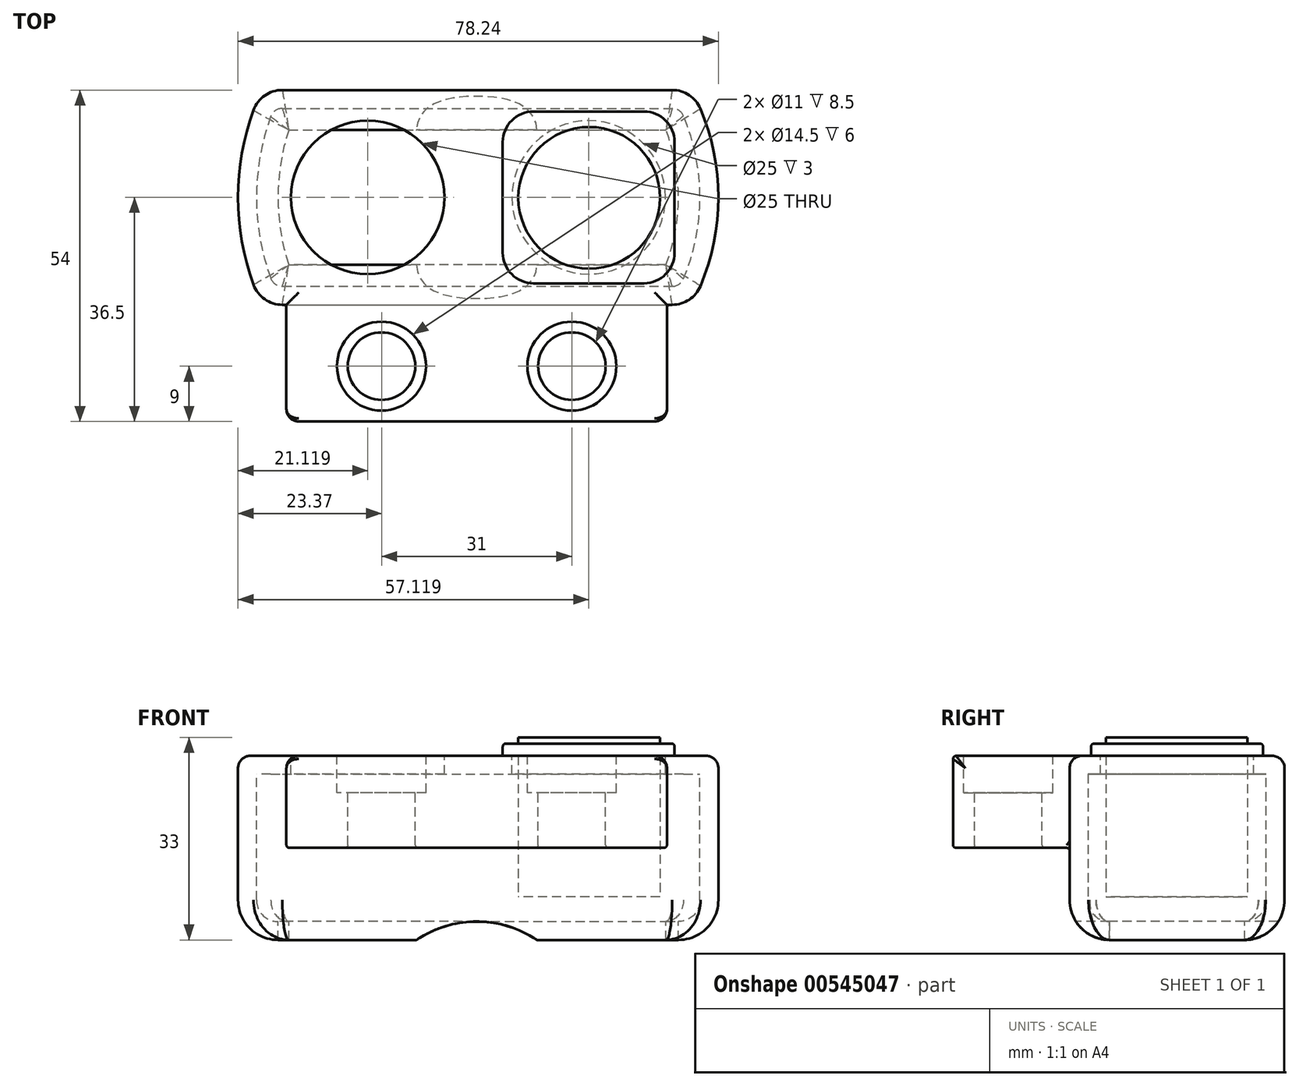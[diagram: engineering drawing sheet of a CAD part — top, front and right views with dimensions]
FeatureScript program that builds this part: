
annotation { "Feature Type Name" : "Feature", "Feature Type Description" : "" }
export const myFeature = defineFeature(function(context is Context, id is Id, definition is map)
    precondition{}
    {
        {
            var Q0;
            Q0=qCreatedBy(makeId("Front.planeOp"),FACE);
            var sketch = newSketch(context, id + "F0", { "sketchPlane" : qUnion([Q0])});
            skLineSegment(sketch, "E0.bottom", {"start": v(0, 0) * mm, "end": v(70, 0) * mm});
            skLineSegment(sketch, "E0.top", {"start": v(0, -30) * mm, "end": v(70, -30) * mm});
            skLineSegment(sketch, "E0.left", {"start": v(0, 0) * mm, "end": v(0, -30) * mm});
            skLineSegment(sketch, "E0.right", {"start": v(70, 0) * mm, "end": v(70, -30) * mm});
            skSolve(sketch);
        }
        {
            var Q0;
            Q0=qSketchRegion(id+"F0",true);
            extrude(context, id + "F1", {"entities" : qUnion([Q0]), "depth" : 20 * mm, "offsetDistance" : 25 * mm, "hasSecondDirection" : true, "secondDirectionOppositeDirection" : true, "secondDirectionDepth" : 15 * mm});
        }
        {
            var Q0;
            Q0=makeQuery(id+"F1.opExtrude","SWEPT_FACE",FACE,{"disambiguationData":[OSD([sQuery(id+"F0.wireOp",EDGE,"E0.bottom")])]});
            var sketch = newSketch(context, id + "F2", { "sketchPlane" : qUnion([Q0])});
            skArc(sketch, "E1", {"start": v(0, 15) * mm, "mid": v(-3.87, -2.5) * mm, "end": v(0, -20) * mm});
            skLineSegment(sketch, "E2", {"start": v(0, 15) * mm, "end": v(0, -20) * mm});
            skLineSegment(sketch, "E3", {"start": v(70, 15) * mm, "end": v(70, -20) * mm});
            skArc(sketch, "E4.trimOffspring", {"start": v(70, -20) * mm, "mid": v(74.37, -2.5) * mm, "end": v(70, 15) * mm});
            skSolve(sketch);
        }
        {
            var Q0;
            Q0=qSketchRegion(id+"F2",true);
            extrude(context, id + "F3", {"entities" : qUnion([Q0]), "operationType" : NewBodyOperationType.ADD, "oppositeDirection" : true, "depth" : 30 * mm, "offsetDistance" : 25 * mm});
        }
        {
            var Q0;
            Q0=makeQuery(id+"FqyKaclqLz1FDZU_1.boolean.opBoolean","MERGE",FACE,{"derivedFrom":[makeQuery(id+"F1.opExtrude","SWEPT_FACE",FACE,{"disambiguationData":[OSD([sQuery(id+"F0.wireOp",EDGE,"E0.top")])]}),makeQuery(id+"FqyKaclqLz1FDZU_1.opExtrude","CAP_FACE",FACE,{"disambiguationData":[OSD([sQuery(id+"FIyjTsEw3E9njMs_1.wireOp",EDGE,"glMM5qbk-qYOk-jkf3-kfGg-ePqJmBg5fgPB"),sQuery(id+"FIyjTsEw3E9njMs_1.wireOp",EDGE,"cEUHAI24-cV1s-2wJQ-DF9F-RTduI9zPpPZA")])],"isStart":false}),makeQuery(id+"FqyKaclqLz1FDZU_1.opExtrude","CAP_FACE",FACE,{"disambiguationData":[OSD([sQuery(id+"FIyjTsEw3E9njMs_1.wireOp",EDGE,"fG08fdOo-hFZ7-qGUP-nEzv-jywKs9Jv7XxH"),sQuery(id+"FIyjTsEw3E9njMs_1.wireOp",EDGE,"jPeKVb5Y-i3kR-RX1O-jRN1-yy8WQ1SG1LOX")])],"isStart":false})]});
            fillet(context, id + "F4", {"entities" : qUnion([Q0]), "radius" : 6.5 * mm, "tangentPropagation" : true, "allowEdgeOverflow" : false});
        }
        {
            var Q0;
            Q0=makeQuery(id+"FqyKaclqLz1FDZU_1.boolean.opBoolean","MERGE",FACE,{"derivedFrom":[makeQuery(id+"F1.opExtrude","SWEPT_FACE",FACE,{"disambiguationData":[OSD([sQuery(id+"F0.wireOp",EDGE,"E0.top")])]}),makeQuery(id+"FqyKaclqLz1FDZU_1.opExtrude","CAP_FACE",FACE,{"disambiguationData":[OSD([sQuery(id+"FIyjTsEw3E9njMs_1.wireOp",EDGE,"glMM5qbk-qYOk-jkf3-kfGg-ePqJmBg5fgPB"),sQuery(id+"FIyjTsEw3E9njMs_1.wireOp",EDGE,"cEUHAI24-cV1s-2wJQ-DF9F-RTduI9zPpPZA")])],"isStart":false}),makeQuery(id+"FqyKaclqLz1FDZU_1.opExtrude","CAP_FACE",FACE,{"disambiguationData":[OSD([sQuery(id+"FIyjTsEw3E9njMs_1.wireOp",EDGE,"fG08fdOo-hFZ7-qGUP-nEzv-jywKs9Jv7XxH"),sQuery(id+"FIyjTsEw3E9njMs_1.wireOp",EDGE,"jPeKVb5Y-i3kR-RX1O-jRN1-yy8WQ1SG1LOX")])],"isStart":false})]});
            shell(context, id + "F5", {"entities" : qUnion([Q0]), "thickness" : 3 * mm});
        }
        {
            var Q0;
            Q0=makeQuery(id+"F1.opExtrude","CAP_FACE",FACE,{"disambiguationData":[OSD([sQuery(id+"F0.wireOp",EDGE,"E0.bottom"),sQuery(id+"F0.wireOp",EDGE,"E0.top"),sQuery(id+"F0.wireOp",EDGE,"E0.left"),sQuery(id+"F0.wireOp",EDGE,"E0.right")])],"isStart":false});
            var sketch = newSketch(context, id + "F6", { "sketchPlane" : qUnion([Q0])});
            skLineSegment(sketch, "E5.bottom", {"start": v(4, 0) * mm, "end": v(66, 0) * mm});
            skLineSegment(sketch, "E5.top", {"start": v(4, -15) * mm, "end": v(66, -15) * mm});
            skLineSegment(sketch, "E5.left", {"start": v(4, 0) * mm, "end": v(4, -15) * mm});
            skLineSegment(sketch, "E5.right", {"start": v(66, 0) * mm, "end": v(66, -15) * mm});
            skSolve(sketch);
        }
        {
            var Q0;
            Q0=makeQuery(id+"F6.imprint","IMPRINT",FACE,{"disambiguationData":[TD([[makeQuery(id+"F6.imprint","IMPRINT",EDGE,{"derivedFrom":sQuery(id+"F6.wireOp",EDGE,"E5.bottom")}),-1.0]])]});
            extrude(context, id + "F7", {"entities" : qUnion([Q0]), "operationType" : NewBodyOperationType.ADD, "depth" : 19 * mm, "offsetDistance" : 25 * mm});
        }
        {
            var Q0;
            {var subQ0=sQuery(id+"FIyjTsEw3E9njMs_1.wireOp",EDGE,"jPeKVb5Y-i3kR-RX1O-jRN1-yy8WQ1SG1LOX");var subQ1=sQuery(id+"FIyjTsEw3E9njMs_1.wireOp",EDGE,"fG08fdOo-hFZ7-qGUP-nEzv-jywKs9Jv7XxH");var subQ2=sQuery(id+"F0.wireOp",EDGE,"E0.bottom");Q0=makeQuery(id+"FqyKaclqLz1FDZU_1.boolean.opBoolean","MERGE",EDGE,{"derivedFrom":[makeQuery(id+"F1.opExtrude","CAP_EDGE",EDGE,{"disambiguationData":[OSD([sQuery(id+"F0.wireOp",EDGE,"E0.right")])],"isStart":false}),makeQuery(id+"FqyKaclqLz1FDZU_1.opExtrude","SWEPT_EDGE",EDGE,{"disambiguationData":[OSD([subQ2,subQ1,subQ0]),TDD([makeQuery(id+"FIyjTsEw3E9njMs_1.imprint","INTERSECT",VERTEX,{"derivedFrom":[makeQuery(id+"F2.imprint","IMPRINT",EDGE,{"derivedFrom":makeQuery(id+"F1.opExtrude","CAP_EDGE",EDGE,{"disambiguationData":[OSD([subQ2])],"isStart":false})}),subQ1,subQ0]})])]})]});}
            var Q1;
            {var subQ0=sQuery(id+"FIyjTsEw3E9njMs_1.wireOp",EDGE,"cEUHAI24-cV1s-2wJQ-DF9F-RTduI9zPpPZA");var subQ1=sQuery(id+"FIyjTsEw3E9njMs_1.wireOp",EDGE,"glMM5qbk-qYOk-jkf3-kfGg-ePqJmBg5fgPB");var subQ2=sQuery(id+"F0.wireOp",EDGE,"E0.bottom");Q1=makeQuery(id+"FqyKaclqLz1FDZU_1.boolean.opBoolean","MERGE",EDGE,{"derivedFrom":[makeQuery(id+"F1.opExtrude","CAP_EDGE",EDGE,{"disambiguationData":[OSD([sQuery(id+"F0.wireOp",EDGE,"E0.left")])],"isStart":false}),makeQuery(id+"FqyKaclqLz1FDZU_1.opExtrude","SWEPT_EDGE",EDGE,{"disambiguationData":[OSD([subQ2,subQ1,subQ0]),TDD([makeQuery(id+"FIyjTsEw3E9njMs_1.imprint","INTERSECT",VERTEX,{"derivedFrom":[makeQuery(id+"F2.imprint","IMPRINT",EDGE,{"derivedFrom":makeQuery(id+"F1.opExtrude","CAP_EDGE",EDGE,{"disambiguationData":[OSD([subQ2])],"isStart":false})}),subQ1,subQ0]})])]})]});}
            var Q2;
            {var subQ0=sQuery(id+"FIyjTsEw3E9njMs_1.wireOp",EDGE,"jPeKVb5Y-i3kR-RX1O-jRN1-yy8WQ1SG1LOX");var subQ1=sQuery(id+"FIyjTsEw3E9njMs_1.wireOp",EDGE,"fG08fdOo-hFZ7-qGUP-nEzv-jywKs9Jv7XxH");var subQ2=sQuery(id+"F0.wireOp",EDGE,"E0.bottom");Q2=makeQuery(id+"FqyKaclqLz1FDZU_1.boolean.opBoolean","MERGE",EDGE,{"derivedFrom":[makeQuery(id+"F1.opExtrude","CAP_EDGE",EDGE,{"disambiguationData":[OSD([sQuery(id+"F0.wireOp",EDGE,"E0.right")])],"isStart":true}),makeQuery(id+"FqyKaclqLz1FDZU_1.opExtrude","SWEPT_EDGE",EDGE,{"disambiguationData":[OSD([subQ2,subQ1,subQ0]),TDD([makeQuery(id+"FIyjTsEw3E9njMs_1.imprint","INTERSECT",VERTEX,{"derivedFrom":[makeQuery(id+"F2.imprint","IMPRINT",EDGE,{"derivedFrom":makeQuery(id+"F1.opExtrude","CAP_EDGE",EDGE,{"disambiguationData":[OSD([subQ2])],"isStart":true})}),subQ1,subQ0]})])]})]});}
            var Q3;
            {var subQ0=sQuery(id+"FIyjTsEw3E9njMs_1.wireOp",EDGE,"cEUHAI24-cV1s-2wJQ-DF9F-RTduI9zPpPZA");var subQ1=sQuery(id+"FIyjTsEw3E9njMs_1.wireOp",EDGE,"glMM5qbk-qYOk-jkf3-kfGg-ePqJmBg5fgPB");var subQ2=sQuery(id+"F0.wireOp",EDGE,"E0.bottom");Q3=makeQuery(id+"FqyKaclqLz1FDZU_1.boolean.opBoolean","MERGE",EDGE,{"derivedFrom":[makeQuery(id+"F1.opExtrude","CAP_EDGE",EDGE,{"disambiguationData":[OSD([sQuery(id+"F0.wireOp",EDGE,"E0.left")])],"isStart":true}),makeQuery(id+"FqyKaclqLz1FDZU_1.opExtrude","SWEPT_EDGE",EDGE,{"disambiguationData":[OSD([subQ2,subQ1,subQ0]),TDD([makeQuery(id+"FIyjTsEw3E9njMs_1.imprint","INTERSECT",VERTEX,{"derivedFrom":[makeQuery(id+"F2.imprint","IMPRINT",EDGE,{"derivedFrom":makeQuery(id+"F1.opExtrude","CAP_EDGE",EDGE,{"disambiguationData":[OSD([subQ2])],"isStart":true})}),subQ1,subQ0]})])]})]});}
            fillet(context, id + "F8", {"entities" : qUnion([Q0, Q1, Q2, Q3]), "radius" : 5 * mm, "tangentPropagation" : true, "allowEdgeOverflow" : false});
        }
        {
            var Q0;
            Q0=makeQuery(id+"FUNl6TjWTGiayeX_1.boolean.opBoolean","MERGE",FACE,{"derivedFrom":[makeQuery(id+"FqyKaclqLz1FDZU_1.boolean.opBoolean","MERGE",FACE,{"derivedFrom":[makeQuery(id+"F1.opExtrude","SWEPT_FACE",FACE,{"disambiguationData":[OSD([sQuery(id+"F0.wireOp",EDGE,"E0.bottom")])]}),makeQuery(id+"FqyKaclqLz1FDZU_1.opExtrude","CAP_FACE",FACE,{"disambiguationData":[OSD([sQuery(id+"FIyjTsEw3E9njMs_1.wireOp",EDGE,"glMM5qbk-qYOk-jkf3-kfGg-ePqJmBg5fgPB"),sQuery(id+"FIyjTsEw3E9njMs_1.wireOp",EDGE,"cEUHAI24-cV1s-2wJQ-DF9F-RTduI9zPpPZA")])],"isStart":true}),makeQuery(id+"FqyKaclqLz1FDZU_1.opExtrude","CAP_FACE",FACE,{"disambiguationData":[OSD([sQuery(id+"FIyjTsEw3E9njMs_1.wireOp",EDGE,"fG08fdOo-hFZ7-qGUP-nEzv-jywKs9Jv7XxH"),sQuery(id+"FIyjTsEw3E9njMs_1.wireOp",EDGE,"jPeKVb5Y-i3kR-RX1O-jRN1-yy8WQ1SG1LOX")])],"isStart":true})]}),makeQuery(id+"FUNl6TjWTGiayeX_1.opExtrude","SWEPT_FACE",FACE,{"disambiguationData":[OSD([sQuery(id+"Fp4lW6qHkl5UULX_1.wireOp",EDGE,"Grlhg8hl-7fqz-5gtc-eQS2-KlK7X2J6LcNq.bottom")])]})]});
            var sketch = newSketch(context, id + "F9", { "sketchPlane" : qUnion([Q0])});
            skPoint(sketch, "E6", {"position": v(19.5, -30) * mm});
            skPoint(sketch, "E7", {"position": v(50.5, -30) * mm});
            skLineSegment(sketch, "E8", {"start": v(66, -30) * mm, "end": v(50.5, -30) * mm});
            skLineSegment(sketch, "E9.trimOffspring", {"start": v(19.5, -30) * mm, "end": v(4, -30) * mm});
            skSolve(sketch);
        }
        {
            var Q0;
            Q0=sQuery(id+"F9.wireOp",VERTEX,"E6");
            var Q1;
            Q1=sQuery(id+"F9.wireOp",VERTEX,"E7");
            var Q2;
            Q2=makeQuery(id+"F1.opExtrude","SWEPT_BODY",BODY,{"disambiguationData":[OSD([sQuery(id+"F0.wireOp",EDGE,"E0.bottom"),sQuery(id+"F0.wireOp",EDGE,"E0.top"),sQuery(id+"F0.wireOp",EDGE,"E0.left"),sQuery(id+"F0.wireOp",EDGE,"E0.right")])]});
            hole(context, id + "F10", {"style" : HoleStyle.C_BORE, "endStyle" : HoleEndStyle.THROUGH, "holeDiameter" : 11 * mm, "cBoreDiameter" : 14.5 * mm, "cBoreDepth" : 6 * mm, "isTappedThrough" : true, "tappedDepth" : 12 * mm, "tapClearance" : 3, "startFromSketch" : true, "locations" : qUnion([Q0, Q1]), "scope" : qUnion([Q2])});
        }
        {
            var Q0;
            {var subQ0=sQuery(id+"F0.wireOp",EDGE,"E0.bottom");Q0=makeQuery(id+"F2.imprint","IMPRINT",FACE,{"disambiguationData":[TD([[makeQuery(id+"F2.imprint","IMPRINT",EDGE,{"derivedFrom":makeQuery(id+"F1.opExtrude","CAP_EDGE",EDGE,{"disambiguationData":[OSD([subQ0])],"isStart":true})}),-1.0]])]});}
            var sketch = newSketch(context, id + "F11", { "sketchPlane" : qUnion([Q0])});
            skLineSegment(sketch, "E10", {"start": v(-3.87, -2.5) * mm, "end": v(17.25, -2.5) * mm});
            skPoint(sketch, "E11", {"position": v(17.25, -2.5) * mm});
            skPoint(sketch, "E12", {"position": v(53.25, -2.5) * mm});
            skLineSegment(sketch, "E13.trimOffspring", {"start": v(53.25, -2.5) * mm, "end": v(74.37, -2.5) * mm});
            skSolve(sketch);
        }
        {
            var Q0;
            Q0=sQuery(id+"F11.wireOp",VERTEX,"E11");
            var Q1;
            Q1=sQuery(id+"F11.wireOp",VERTEX,"E12");
            var Q2;
            Q2=makeQuery(id+"F1.opExtrude","SWEPT_BODY",BODY,{"disambiguationData":[OSD([sQuery(id+"F0.wireOp",EDGE,"E0.bottom"),sQuery(id+"F0.wireOp",EDGE,"E0.top"),sQuery(id+"F0.wireOp",EDGE,"E0.left"),sQuery(id+"F0.wireOp",EDGE,"E0.right")])]});
            hole(context, id + "F12", {"style" : HoleStyle.SIMPLE, "endStyle" : HoleEndStyle.BLIND, "holeDiameter" : 25 * mm, "holeDepth" : 10 * mm, "isTappedThrough" : true, "tappedDepth" : 12 * mm, "tapClearance" : 3, "startFromSketch" : true, "locations" : qUnion([Q0, Q1]), "scope" : qUnion([Q2])});
        }
        {
            var Q0;
            Q0=makeQuery(id+"F1.opExtrude","CAP_FACE",FACE,{"disambiguationData":[OSD([sQuery(id+"F0.wireOp",EDGE,"E0.bottom"),sQuery(id+"F0.wireOp",EDGE,"E0.top"),sQuery(id+"F0.wireOp",EDGE,"E0.left"),sQuery(id+"F0.wireOp",EDGE,"E0.right")])],"isStart":false});
            var sketch = newSketch(context, id + "F13", { "sketchPlane" : qUnion([Q0])});
            skPoint(sketch, "E14", {"position": v(35, -44.5) * mm});
            skLineSegment(sketch, "E15", {"start": v(35, 0) * mm, "end": v(35, -44.5) * mm});
            skSolve(sketch);
        }
        {
            var Q0;
            Q0=sQuery(id+"F13.wireOp",VERTEX,"E14");
            var Q1;
            Q1=makeQuery(id+"F1.opExtrude","SWEPT_BODY",BODY,{"disambiguationData":[OSD([sQuery(id+"F0.wireOp",EDGE,"E0.bottom"),sQuery(id+"F0.wireOp",EDGE,"E0.top"),sQuery(id+"F0.wireOp",EDGE,"E0.left"),sQuery(id+"F0.wireOp",EDGE,"E0.right")])]});
            hole(context, id + "F14", {"style" : HoleStyle.SIMPLE, "endStyle" : HoleEndStyle.THROUGH, "holeDiameter" : 35 * mm, "isTappedThrough" : true, "tappedDepth" : 12 * mm, "tapClearance" : 3, "startFromSketch" : true, "locations" : qUnion([Q0]), "scope" : qUnion([Q1])});
        }
        {
            var Q0;
            Q0=makeQuery(id+"F10.hole-0.boolean.opBoolean","COPY",EDGE,{"derivedFrom":makeQuery(id+"F10.hole-0.opRevolve","SWEPT_EDGE",EDGE,{"disambiguationData":[OSD([sQuery(id+"F10.hole-0.sketch.wireOp",EDGE,"cbore_start_line_2"),sQuery(id+"F10.hole-0.sketch.wireOp",EDGE,"cbore_start_line_3")])]})});
            var Q1;
            Q1=makeQuery(id+"F7.opExtrude","CAP_EDGE",EDGE,{"disambiguationData":[OSD([sQuery(id+"F6.wireOp",EDGE,"E5.bottom")])],"isStart":false});
            var Q2;
            Q2=makeQuery(id+"F10.hole-1.boolean.opBoolean","INTERSECT",EDGE,{"derivedFrom":[makeQuery(id+"F7.opExtrude","SWEPT_FACE",FACE,{"disambiguationData":[OSD([sQuery(id+"F6.wireOp",EDGE,"E5.top")])]}),makeQuery(id+"F10.hole-1.opRevolve","SWEPT_FACE",FACE,{"disambiguationData":[OSD([sQuery(id+"F10.hole-1.sketch.wireOp",EDGE,"core_line_2")])]})]});
            var Q3;
            Q3=makeQuery(id+"F7.opExtrude","CAP_EDGE",EDGE,{"disambiguationData":[OSD([sQuery(id+"F6.wireOp",EDGE,"E5.top")])],"isStart":false});
            var Q4;
            Q4=makeQuery(id+"F7.opExtrude","SWEPT_FACE",FACE,{"disambiguationData":[OSD([sQuery(id+"F6.wireOp",EDGE,"E5.top")])]});
            var Q5;
            Q5=makeQuery(id+"F12.hole-0.boolean.opBoolean","COPY",EDGE,{"derivedFrom":makeQuery(id+"F12.hole-0.opRevolve","SWEPT_EDGE",EDGE,{"disambiguationData":[OSD([sQuery(id+"F12.hole-0.sketch.wireOp",EDGE,"core_line_2"),sQuery(id+"F12.hole-0.sketch.wireOp",EDGE,"core_line_3")])]})});
            var Q6;
            Q6=makeQuery(id+"F12.hole-1.boolean.opBoolean","COPY",EDGE,{"derivedFrom":makeQuery(id+"F12.hole-1.opRevolve","SWEPT_EDGE",EDGE,{"disambiguationData":[OSD([sQuery(id+"F12.hole-1.sketch.wireOp",EDGE,"core_line_2"),sQuery(id+"F12.hole-1.sketch.wireOp",EDGE,"core_line_3")])]})});
            var Q7;
            Q7=makeQuery(id+"F10.hole-1.boolean.opBoolean","COPY",EDGE,{"derivedFrom":makeQuery(id+"F10.hole-1.opRevolve","SWEPT_EDGE",EDGE,{"disambiguationData":[OSD([sQuery(id+"F10.hole-1.sketch.wireOp",EDGE,"cbore_start_line_2"),sQuery(id+"F10.hole-1.sketch.wireOp",EDGE,"cbore_start_line_3")])]})});
            var Q8;
            Q8=makeQuery(id+"F12.hole-0.boolean.opBoolean","INTERSECT",EDGE,{"derivedFrom":[makeQuery(id+"F5.opShell","OFFSET_FACE",FACE,{"disambiguationData":[OSD([sQuery(id+"F0.wireOp",EDGE,"E0.bottom"),sQuery(id+"F2.wireOp",EDGE,"E1"),sQuery(id+"F2.wireOp",EDGE,"E2"),sQuery(id+"F2.wireOp",EDGE,"E3"),sQuery(id+"F2.wireOp",EDGE,"E4.trimOffspring")])]}),makeQuery(id+"F12.hole-0.opRevolve","SWEPT_FACE",FACE,{"disambiguationData":[OSD([sQuery(id+"F12.hole-0.sketch.wireOp",EDGE,"core_line_2")])]})]});
            var Q9;
            Q9=makeQuery(id+"F12.hole-1.boolean.opBoolean","INTERSECT",EDGE,{"derivedFrom":[makeQuery(id+"F5.opShell","OFFSET_FACE",FACE,{"disambiguationData":[OSD([sQuery(id+"F0.wireOp",EDGE,"E0.bottom"),sQuery(id+"F2.wireOp",EDGE,"E1"),sQuery(id+"F2.wireOp",EDGE,"E2"),sQuery(id+"F2.wireOp",EDGE,"E3"),sQuery(id+"F2.wireOp",EDGE,"E4.trimOffspring")])]}),makeQuery(id+"F12.hole-1.opRevolve","SWEPT_FACE",FACE,{"disambiguationData":[OSD([sQuery(id+"F12.hole-1.sketch.wireOp",EDGE,"core_line_2")])]})]});
            var Q10;
            Q10=makeQuery(id+"F10.hole-1.boolean.opBoolean","COPY",EDGE,{"derivedFrom":makeQuery(id+"F10.hole-1.opRevolve","SWEPT_EDGE",EDGE,{"disambiguationData":[OSD([sQuery(id+"F10.hole-1.sketch.wireOp",EDGE,"cbore_start_line_1"),sQuery(id+"F10.hole-1.sketch.wireOp",EDGE,"core_line_2")])]})});
            fillet(context, id + "F15", {"entities" : qUnion([Q0, Q1, Q2, Q3, Q4, Q5, Q6, Q7, Q8, Q9, Q10]), "radius" : .5 * mm, "tangentPropagation" : true, "allowEdgeOverflow" : false});
        }
        {
            var Q0;
            {var subQ0=sQuery(id+"FIyjTsEw3E9njMs_1.wireOp",EDGE,"cEUHAI24-cV1s-2wJQ-DF9F-RTduI9zPpPZA");var subQ1=sQuery(id+"FIyjTsEw3E9njMs_1.wireOp",EDGE,"glMM5qbk-qYOk-jkf3-kfGg-ePqJmBg5fgPB");var subQ2=sQuery(id+"F0.wireOp",EDGE,"E0.bottom");var subQ3=sQuery(id+"F0.wireOp",EDGE,"E0.left");Q0=makeQuery(id+"F5.opShell","OFFSET_EDGE",EDGE,{"disambiguationData":[OSD([subQ2,subQ3,subQ1,subQ0]),TDD([makeQuery(id+"FqyKaclqLz1FDZU_1.boolean.opBoolean","MERGE",EDGE,{"derivedFrom":[makeQuery(id+"F1.opExtrude","CAP_EDGE",EDGE,{"disambiguationData":[OSD([subQ3])],"isStart":true}),makeQuery(id+"FqyKaclqLz1FDZU_1.opExtrude","SWEPT_EDGE",EDGE,{"disambiguationData":[OSD([subQ2,subQ1,subQ0]),TDD([makeQuery(id+"FIyjTsEw3E9njMs_1.imprint","INTERSECT",VERTEX,{"derivedFrom":[makeQuery(id+"F2.imprint","IMPRINT",EDGE,{"derivedFrom":makeQuery(id+"F1.opExtrude","CAP_EDGE",EDGE,{"disambiguationData":[OSD([subQ2])],"isStart":true})}),subQ1,subQ0]})])]})]})])]});}
            var Q1;
            {var subQ0=sQuery(id+"FIyjTsEw3E9njMs_1.wireOp",EDGE,"glMM5qbk-qYOk-jkf3-kfGg-ePqJmBg5fgPB");Q1=makeQuery(id+"F5.opShell","OFFSET_FACE",FACE,{"disambiguationData":[OSD([subQ0]),TDD([makeQuery(id+"FqyKaclqLz1FDZU_1.opExtrude","SWEPT_FACE",FACE,{"disambiguationData":[OSD([subQ0])]})])]});}
            var Q2;
            {var subQ0=sQuery(id+"FIyjTsEw3E9njMs_1.wireOp",EDGE,"fG08fdOo-hFZ7-qGUP-nEzv-jywKs9Jv7XxH");Q2=makeQuery(id+"F5.opShell","OFFSET_FACE",FACE,{"disambiguationData":[OSD([subQ0]),TDD([makeQuery(id+"FqyKaclqLz1FDZU_1.opExtrude","SWEPT_FACE",FACE,{"disambiguationData":[OSD([subQ0])]})])]});}
            var Q3;
            {var subQ0=sQuery(id+"F2.wireOp",EDGE,"E4.trimOffspring");var subQ1=sQuery(id+"F2.wireOp",EDGE,"E3");var subQ2=sQuery(id+"F0.wireOp",EDGE,"E0.bottom");var subQ3=sQuery(id+"F0.wireOp",EDGE,"E0.right");Q3=makeQuery(id+"F5.opShell","OFFSET_EDGE",EDGE,{"disambiguationData":[OSD([subQ2,subQ3,subQ1,subQ0]),TDD([makeQuery(id+"F3.boolean.opBoolean","MERGE",EDGE,{"derivedFrom":[makeQuery(id+"F1.opExtrude","CAP_EDGE",EDGE,{"disambiguationData":[OSD([subQ3])],"isStart":false}),makeQuery(id+"F3.opExtrude","SWEPT_EDGE",EDGE,{"disambiguationData":[OSD([subQ2,subQ1,subQ0]),TDD([makeQuery(id+"F2.imprint","INTERSECT",VERTEX,{"derivedFrom":[makeQuery(id+"F1.opExtrude","CAP_EDGE",EDGE,{"disambiguationData":[OSD([subQ2])],"isStart":false}),subQ1,subQ0]})])]})]})])]});}
            var Q4;
            {var subQ0=sQuery(id+"F2.wireOp",EDGE,"E4.trimOffspring");var subQ1=sQuery(id+"F2.wireOp",EDGE,"E3");var subQ2=sQuery(id+"F0.wireOp",EDGE,"E0.bottom");var subQ3=sQuery(id+"F0.wireOp",EDGE,"E0.right");Q4=makeQuery(id+"F5.opShell","OFFSET_EDGE",EDGE,{"disambiguationData":[OSD([subQ2,subQ3,subQ1,subQ0]),TDD([makeQuery(id+"F3.boolean.opBoolean","MERGE",EDGE,{"derivedFrom":[makeQuery(id+"F1.opExtrude","CAP_EDGE",EDGE,{"disambiguationData":[OSD([subQ3])],"isStart":true}),makeQuery(id+"F3.opExtrude","SWEPT_EDGE",EDGE,{"disambiguationData":[OSD([subQ2,subQ1,subQ0]),TDD([makeQuery(id+"F2.imprint","INTERSECT",VERTEX,{"derivedFrom":[makeQuery(id+"F1.opExtrude","CAP_EDGE",EDGE,{"disambiguationData":[OSD([subQ2])],"isStart":true}),subQ1,subQ0]})])]})]})])]});}
            var Q5;
            {var subQ0=sQuery(id+"F2.wireOp",EDGE,"E2");var subQ1=sQuery(id+"F2.wireOp",EDGE,"E1");var subQ2=sQuery(id+"F0.wireOp",EDGE,"E0.bottom");var subQ3=sQuery(id+"F0.wireOp",EDGE,"E0.left");Q5=makeQuery(id+"F5.opShell","OFFSET_EDGE",EDGE,{"disambiguationData":[OSD([subQ2,subQ3,subQ1,subQ0]),TDD([makeQuery(id+"F3.boolean.opBoolean","MERGE",EDGE,{"derivedFrom":[makeQuery(id+"F1.opExtrude","CAP_EDGE",EDGE,{"disambiguationData":[OSD([subQ3])],"isStart":false}),makeQuery(id+"F3.opExtrude","SWEPT_EDGE",EDGE,{"disambiguationData":[OSD([subQ2,subQ1,subQ0]),TDD([makeQuery(id+"F2.imprint","INTERSECT",VERTEX,{"derivedFrom":[makeQuery(id+"F1.opExtrude","CAP_EDGE",EDGE,{"disambiguationData":[OSD([subQ2])],"isStart":false}),subQ1,subQ0]})])]})]})])]});}
            fillet(context, id + "F16", {"entities" : qUnion([Q0, Q1, Q2, Q3, Q4, Q5]), "radius" : 2 * mm, "tangentPropagation" : true, "allowEdgeOverflow" : false});
        }
        {
            var Q0;
            Q0=makeQuery(id+"F7.opExtrude","SWEPT_EDGE",EDGE,{"disambiguationData":[OSD([sQuery(id+"F0.wireOp",EDGE,"E0.bottom"),sQuery(id+"F6.wireOp",EDGE,"E5.bottom"),sQuery(id+"F6.wireOp",EDGE,"E5.right")])]});
            var Q1;
            {var subQ0=sQuery(id+"F2.wireOp",EDGE,"E4.trimOffspring");var subQ1=sQuery(id+"F0.wireOp",EDGE,"E0.bottom");Q1=makeQuery(id+"F7.boolean.opBoolean","SPLIT",EDGE,{"disambiguationData":[TD([makeQuery(id+"F3.opExtrude","SWEPT_FACE",FACE,{"disambiguationData":[OSD([subQ0])]})])],"derivedFrom":makeQuery(id+"F1.opExtrude","CAP_EDGE",EDGE,{"disambiguationData":[OSD([subQ1])],"isStart":false})});}
            var Q2;
            Q2=makeQuery(id+"F7.opExtrude","SWEPT_EDGE",EDGE,{"disambiguationData":[OSD([sQuery(id+"F0.wireOp",EDGE,"E0.bottom"),sQuery(id+"F6.wireOp",EDGE,"E5.bottom"),sQuery(id+"F6.wireOp",EDGE,"E5.left")])]});
            fillet(context, id + "F17", {"entities" : qUnion([Q0, Q1, Q2]), "radius" : 2 * mm, "tangentPropagation" : true, "allowEdgeOverflow" : false});
        }
        {
            var Q0;
            Q0=makeQuery(id+"F7.boolean.opBoolean","MERGE",FACE,{"derivedFrom":[makeQuery(id+"FqyKaclqLz1FDZU_1.boolean.opBoolean","MERGE",FACE,{"derivedFrom":[makeQuery(id+"F1.opExtrude","SWEPT_FACE",FACE,{"disambiguationData":[OSD([sQuery(id+"F0.wireOp",EDGE,"E0.bottom")])]}),makeQuery(id+"FqyKaclqLz1FDZU_1.opExtrude","CAP_FACE",FACE,{"disambiguationData":[OSD([sQuery(id+"FIyjTsEw3E9njMs_1.wireOp",EDGE,"glMM5qbk-qYOk-jkf3-kfGg-ePqJmBg5fgPB"),sQuery(id+"FIyjTsEw3E9njMs_1.wireOp",EDGE,"cEUHAI24-cV1s-2wJQ-DF9F-RTduI9zPpPZA")])],"isStart":true}),makeQuery(id+"FqyKaclqLz1FDZU_1.opExtrude","CAP_FACE",FACE,{"disambiguationData":[OSD([sQuery(id+"FIyjTsEw3E9njMs_1.wireOp",EDGE,"fG08fdOo-hFZ7-qGUP-nEzv-jywKs9Jv7XxH"),sQuery(id+"FIyjTsEw3E9njMs_1.wireOp",EDGE,"jPeKVb5Y-i3kR-RX1O-jRN1-yy8WQ1SG1LOX")])],"isStart":true})]}),makeQuery(id+"F7.opExtrude","SWEPT_FACE",FACE,{"disambiguationData":[OSD([sQuery(id+"F6.wireOp",EDGE,"E5.bottom")])]})]});
            var sketch = newSketch(context, id + "F18", { "sketchPlane" : qUnion([Q0])});
            skLineSegment(sketch, "E16.bottom", {"start": v(39.25, 11.5) * mm, "end": v(67.25, 11.5) * mm});
            skLineSegment(sketch, "E16.top", {"start": v(39.25, -16.5) * mm, "end": v(67.25, -16.5) * mm});
            skLineSegment(sketch, "E16.left", {"start": v(39.25, 11.5) * mm, "end": v(39.25, -16.5) * mm});
            skLineSegment(sketch, "E16.right", {"start": v(67.25, 11.5) * mm, "end": v(67.25, -16.5) * mm});
            skCircle(sketch, "E17", {"center": v(53.25, -2.5) * mm, "radius": 14 * mm});
            skSolve(sketch);
        }
        {
            var Q0;
            Q0=qSketchRegion(id+"F18",true);
            extrude(context, id + "F19", {"entities" : qUnion([Q0]), "operationType" : NewBodyOperationType.ADD, "depth" : 2 * mm, "offsetDistance" : 25 * mm});
        }
        {
            var Q0;
            Q0=makeQuery(id+"F19.opExtrude","SWEPT_EDGE",EDGE,{"disambiguationData":[OSD([sQuery(id+"F18.wireOp",EDGE,"E16.top"),sQuery(id+"F18.wireOp",EDGE,"E16.right")])]});
            var Q1;
            Q1=makeQuery(id+"F19.opExtrude","SWEPT_EDGE",EDGE,{"disambiguationData":[OSD([sQuery(id+"F18.wireOp",EDGE,"E16.top"),sQuery(id+"F18.wireOp",EDGE,"E16.left")])]});
            var Q2;
            Q2=makeQuery(id+"F19.opExtrude","SWEPT_EDGE",EDGE,{"disambiguationData":[OSD([sQuery(id+"F18.wireOp",EDGE,"E16.bottom"),sQuery(id+"F18.wireOp",EDGE,"E16.right")])]});
            var Q3;
            Q3=makeQuery(id+"F19.opExtrude","SWEPT_EDGE",EDGE,{"disambiguationData":[OSD([sQuery(id+"F18.wireOp",EDGE,"E16.bottom"),sQuery(id+"F18.wireOp",EDGE,"E16.left")])]});
            fillet(context, id + "F20", {"entities" : qUnion([Q0, Q1, Q2, Q3]), "radius" : 5 * mm, "tangentPropagation" : true, "allowEdgeOverflow" : false});
        }
        {
            var Q0;
            Q0=makeQuery(id+"F19.opExtrude","CAP_FACE",FACE,{"disambiguationData":[OSD([sQuery(id+"F18.wireOp",EDGE,"E16.bottom"),sQuery(id+"F18.wireOp",EDGE,"E16.top"),sQuery(id+"F18.wireOp",EDGE,"E16.left"),sQuery(id+"F18.wireOp",EDGE,"E16.right")])],"isStart":false});
            fillet(context, id + "F21", {"entities" : qUnion([Q0]), "radius" : .5 * mm, "tangentPropagation" : true, "allowEdgeOverflow" : false});
        }
        {
            var Q0;
            Q0=makeQuery(id+"F19.opExtrude","CAP_FACE",FACE,{"disambiguationData":[OSD([sQuery(id+"F18.wireOp",EDGE,"E16.bottom"),sQuery(id+"F18.wireOp",EDGE,"E16.top"),sQuery(id+"F18.wireOp",EDGE,"E16.left"),sQuery(id+"F18.wireOp",EDGE,"E16.right")])],"isStart":false});
            var sketch = newSketch(context, id + "F22", { "sketchPlane" : qUnion([Q0])});
            skLineSegment(sketch, "E18", {"start": v(62.25, 6.5) * mm, "end": v(43.94, -12.14) * mm});
            skLineSegment(sketch, "E19", {"start": v(41.07, 9.68) * mm, "end": v(65.43, -14.68) * mm});
            skCircle(sketch, "E20", {"center": v(53.33, -2.58) * mm, "radius": 11.54 * mm});
            skSolve(sketch);
        }
        {
            var Q0;
            Q0=qSketchRegion(id+"F22",true);
            extrude(context, id + "F23", {"entities" : qUnion([Q0]), "operationType" : NewBodyOperationType.ADD, "depth" : 1 * mm, "offsetDistance" : 25 * mm, "hasSecondDirection" : true, "secondDirectionOppositeDirection" : true, "secondDirectionDepth" : 25 * mm});
        }
    });
